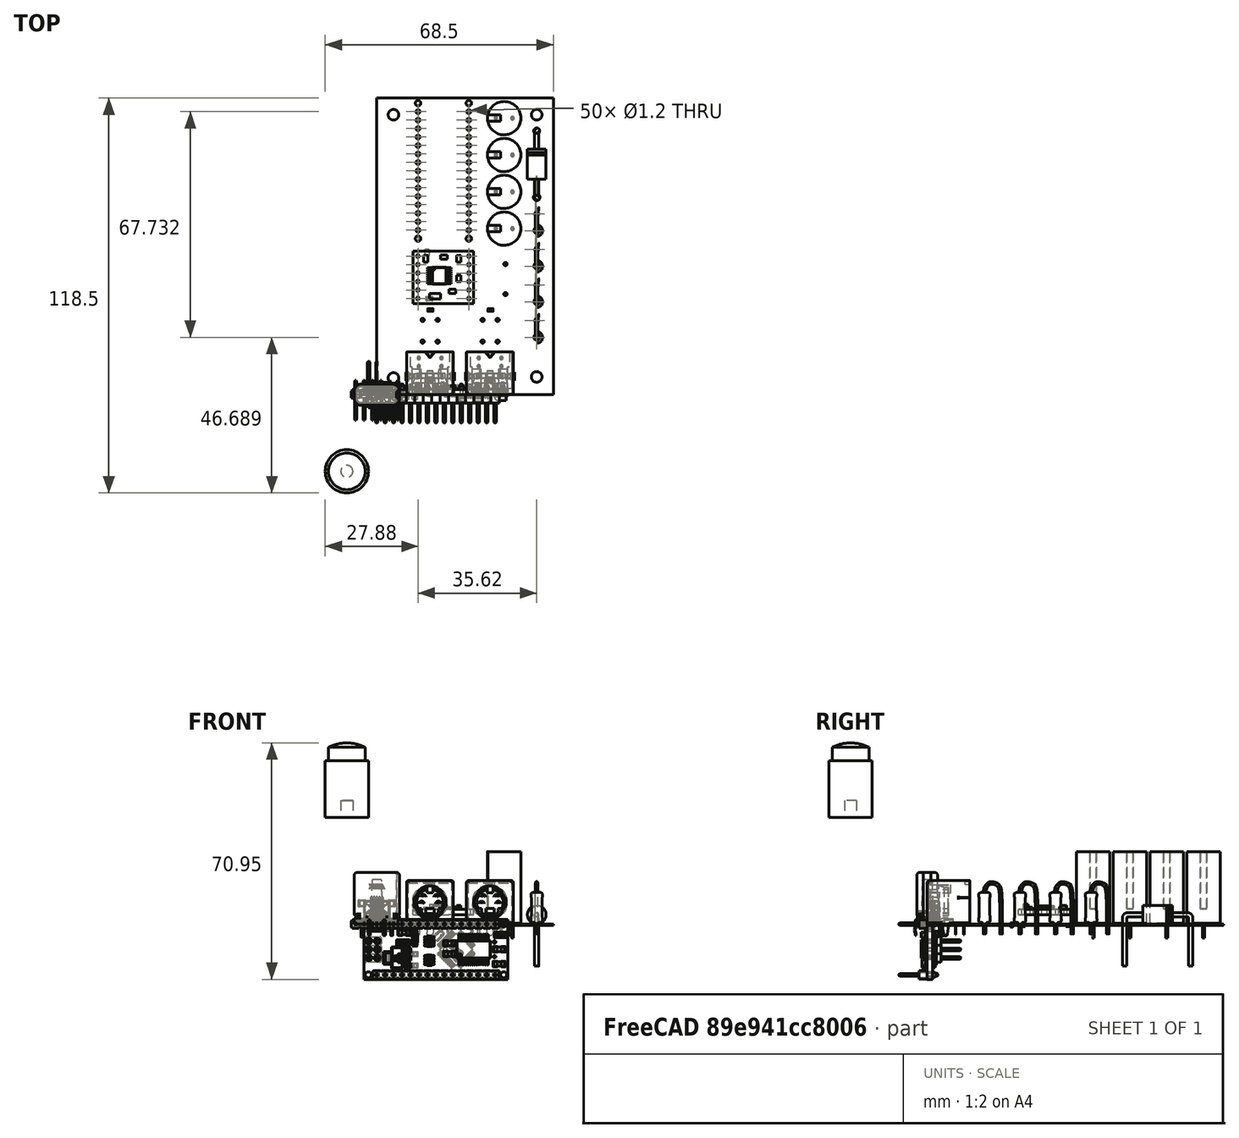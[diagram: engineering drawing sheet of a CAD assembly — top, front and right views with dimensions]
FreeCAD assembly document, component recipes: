
FREECAD ASSEMBLY — COMPONENT RECIPES ("box")

This assembly document has 7 components, labeled P0..P6 below (a component is one placed body or linked part). 6 of them carry a construction recipe — the FreeCAD feature program that regenerates the part from scratch, quoted from this document or its linked companion documents; the rest are supplied as boundary geometry only. No exploded tour is included for this assembly.
COMPONENT P0 — recipe-attached ("Back001", modeled in this document).
Construction recipe (the document's own serialized feature program — sketch geometry with constraints, then the solid features built on it; lengths are millimeters unless a unit is written):

FEATURE [PartDesign::Plane] DatumPlane001
  AttachmentSupport = -> [Mirrored002]
  Length = 77.6965
  MapMode = 5
  Placement = pos=(0,-47,-3.95e-14) rot=(1,0,0;1.5708rad)
  ResizeMode = 0
  Width = 74.6965
FEATURE [Sketcher::SketchObject] Sketch010
  ArcFitTolerance = 0
  AttachmentSupport = -> [DatumPlane001]
  FullyConstrained = true
  MakeInternals = false
  MapMode = 5
  Placement = pos=(0,-47,-3.95e-14) rot=(1,0,0;1.5708rad)
  sketch-geometry (8):
    g0: LineSegment StartX=-32.5 StartY=37 StartZ=0 EndX=-32.5 EndY=2 EndZ=0
    g1: LineSegment StartX=-32.5 StartY=2 StartZ=0 EndX=32.5 EndY=2 EndZ=0
    g2: LineSegment StartX=32.5 StartY=2 StartZ=0 EndX=32.5 EndY=37 EndZ=0
    g3: LineSegment StartX=32.5 StartY=37 StartZ=0 EndX=-32.5 EndY=37 EndZ=0
    g4: LineSegment StartX=0 StartY=29 StartZ=0 EndX=0 EndY=19 EndZ=0
    g5: LineSegment StartX=0 StartY=19 StartZ=0 EndX=13 EndY=19 EndZ=0
    g6: LineSegment StartX=13 StartY=19 StartZ=0 EndX=13 EndY=29 EndZ=0
    g7: LineSegment StartX=13 StartY=29 StartZ=0 EndX=0 EndY=29 EndZ=0
  constraints (23):
    c: Coincident(g0,g1)
    c: Coincident(g1,g2)
    c: Coincident(g2,g3)
    c: Coincident(g3,g0)
    c: Vertical(g0)
    c: Vertical(g2)
    c: Horizontal(g1)
    c: Symmetric(g0,g2,g-2)
    c: DistanceY(g-1,g0) = 2
    c: DistanceX(g3,g3) = 65
    c: DistanceY(g0,g0) = 35
    c: Coincident(g4,g5)
    c: Coincident(g5,g6)
    c: Coincident(g6,g7)
    c: Coincident(g7,g4)
    c: Vertical(g4)
    c: Vertical(g6)
    c: Horizontal(g5)
    c: Horizontal(g7)
    c: DistanceX(g7,g7) = 13
    c: DistanceY(g6,g6) = 10
    c: DistanceY(g-1,g4) = 19
    c: PointOnObject(g4,g-2)
FEATURE [PartDesign::Pad] Pad003
  Direction = (0,-1,2e-16)
  Length = 1.5
  Length2 = 10
  Placement = pos=(0,-47,-3.94e-14) rot=(1,0,0;1.5708rad)
  Profile = -> Sketch010
  ReferenceAxis = -> Sketch010 [N_Axis]
  Refine = true
  Suppressed = false
  Type = 0
FEATURE [PartDesign::Fillet] Fillet003
  Base = -> Pad003 [Edge1,Edge8,Edge5,Edge2,Edge13,Edge20,Edge14,Edge17]
  BaseFeature = -> Pad003
  Placement = pos=(0,-47,-3.94e-14) rot=(1,0,0;1.5708rad)
  Radius = 2
  Refine = true
  SupportTransform = false
  Suppressed = false
  UseAllEdges = false
FEATURE [Sketcher::SketchObject] Sketch019
  ArcFitTolerance = 1e-06
  AttachmentSupport = -> [Fillet003]
  FullyConstrained = true
  MakeInternals = false
  MapMode = 5
  Placement = pos=(0,-48.5,-3.94e-14) rot=(1,0,0;1.5708rad)
  sketch-geometry (6):
    g0: ArcOfCircle CenterX=23 CenterY=24 CenterZ=0 NormalX=0 NormalY=0 NormalZ=1 AngleXU=0 Radius=4.8 StartAngle=5.29807 EndAngle=10.4099
    g1: Circle [constr] CenterX=23 CenterY=24 CenterZ=0 NormalX=0 NormalY=0 NormalZ=1 AngleXU=0 Radius=6.325
    g2: LineSegment StartX=20.3467 StartY=20 StartZ=0 EndX=25.6533 EndY=20 EndZ=0
    g3: Circle [constr] CenterX=-23 CenterY=24 CenterZ=0 NormalX=0 NormalY=0 NormalZ=1 AngleXU=0 Radius=6.325
    g4: ArcOfCircle CenterX=-23 CenterY=24 CenterZ=0 NormalX=0 NormalY=0 NormalZ=1 AngleXU=0 Radius=4.8 StartAngle=5.29807 EndAngle=10.4099
    g5: LineSegment StartX=-25.6533 StartY=20 StartZ=0 EndX=-20.3467 EndY=20 EndZ=0
  constraints (18):
    c: Diameter(g0) = 9.6
    c: Diameter(g1) = 12.65
    c: Coincident(g1,g0)
    c: Distance(g0,g2) = 4
    c: DistanceY(g-1,g0) = 24
    c: DistanceX(g-1,g0) = 23
    c: Coincident(g0,g2)
    c: Coincident(g0,g2)
    c: Coincident(g4,g3)
    c: Equal(g4,g0)
    c: Equal(g3,g1)
    c: Horizontal(g3,g0)
    c: Horizontal(g5)
    c: Horizontal(g5,g0)
    c: Coincident(g4,g5)
    c: Coincident(g4,g5)
    c: DistanceX(g3,g-1) = 23
    c: Horizontal(g2)
FEATURE [PartDesign::Pocket] Pocket010
  BaseFeature = -> Fillet003
  Direction = (0,1,-2e-16)
  Length = 5
  Length2 = 5
  Placement = pos=(0,-47,-3.94e-14) rot=(1,0,0;1.5708rad)
  Profile = -> Sketch019
  ReferenceAxis = -> Sketch019 [N_Axis]
  Refine = true
  Suppressed = false
  Type = 1
FEATURE [PartDesign::Body] Body002  label="Back"
  AllowCompound = false
  Group = -> [DatumPlane001,Sketch010,Pad003,Fillet003,Sketch019,Pocket010]
  Origin = -> Origin052
  Tip = -> Pocket010
COMPONENT P1 — recipe-attached ("Bottom001", modeled in this document).
Construction recipe (the document's own serialized feature program — sketch geometry with constraints, then the solid features built on it; lengths are millimeters unless a unit is written):

FEATURE [Sketcher::SketchObject] Sketch
  ArcFitTolerance = 0
  AttachmentSupport = -> [XY_Plane050]
  FullyConstrained = true
  MakeInternals = false
  MapMode = 5
  sketch-geometry (4):
    g0: LineSegment StartX=-35 StartY=51 StartZ=0 EndX=-35 EndY=-51 EndZ=0
    g1: LineSegment StartX=-35 StartY=-51 StartZ=0 EndX=35 EndY=-51 EndZ=0
    g2: LineSegment StartX=35 StartY=-51 StartZ=0 EndX=35 EndY=51 EndZ=0
    g3: LineSegment StartX=35 StartY=51 StartZ=0 EndX=-35 EndY=51 EndZ=0
  constraints (10):
    c: Coincident(g0,g1)
    c: Coincident(g1,g2)
    c: Coincident(g2,g3)
    c: Coincident(g3,g0)
    c: Vertical(g2)
    c: Horizontal(g3)
    c: Distance(g0,g2) = 70
    c: Distance(g1,g3) = 102
    c: Symmetric(g1,g0,g-2)
    c: Symmetric(g0,g0,g-1)
FEATURE [PartDesign::Pad] Pad
  Direction = (0,0,1)
  Length = 20
  Length2 = 10
  Profile = -> Sketch
  ReferenceAxis = -> Sketch [N_Axis]
  Refine = true
  Suppressed = false
  Type = 0
FEATURE [Sketcher::SketchObject] Sketch001
  ArcFitTolerance = 0
  AttachmentSupport = -> [Pad]
  FullyConstrained = true
  MakeInternals = false
  MapMode = 5
  Placement = pos=(0,0,20) rot=(0,0,1;0rad)
  sketch-geometry (4):
    g0: LineSegment StartX=-32.5 StartY=45 StartZ=0 EndX=-32.5 EndY=-45 EndZ=0
    g1: LineSegment StartX=-32.5 StartY=-45 StartZ=0 EndX=32.5 EndY=-45 EndZ=0
    g2: LineSegment StartX=32.5 StartY=-45 StartZ=0 EndX=32.5 EndY=45 EndZ=0
    g3: LineSegment StartX=32.5 StartY=45 StartZ=0 EndX=-32.5 EndY=45 EndZ=0
  constraints (10):
    c: Coincident(g0,g1)
    c: Coincident(g1,g2)
    c: Coincident(g2,g3)
    c: Coincident(g3,g0)
    c: Vertical(g2)
    c: Horizontal(g1)
    c: Symmetric(g0,g2,g-2)
    c: Symmetric(g0,g0,g-1)
    c: DistanceX(g3,g3) = 65
    c: DistanceY(g2,g2) = 90
FEATURE [PartDesign::Pocket] Pocket
  BaseFeature = -> Pad
  Direction = (0,0,-1)
  Length = 18
  Length2 = 5
  Profile = -> Sketch001
  ReferenceAxis = -> Sketch001 [N_Axis]
  Refine = true
  Suppressed = false
  Type = 0
FEATURE [Sketcher::SketchObject] Sketch002
  ArcFitTolerance = 0
  AttachmentSupport = -> [Pocket]
  ExternalGeometry = -> [Pocket]
  FullyConstrained = true
  MakeInternals = false
  MapMode = 5
  Placement = pos=(0,51,0) rot=(0,0.707107,0.707107;3.14159rad)
  sketch-geometry (4):
    g0: LineSegment StartX=-31 StartY=20 StartZ=0 EndX=-31 EndY=4 EndZ=0
    g1: LineSegment StartX=-31 StartY=4 StartZ=0 EndX=31 EndY=4 EndZ=0
    g2: LineSegment StartX=31 StartY=4 StartZ=0 EndX=31 EndY=20 EndZ=0
    g3: LineSegment StartX=31 StartY=20 StartZ=0 EndX=-31 EndY=20 EndZ=0
  constraints (11):
    c: Coincident(g0,g1)
    c: Coincident(g1,g2)
    c: Coincident(g2,g3)
    c: Coincident(g3,g0)
    c: Vertical(g0)
    c: Vertical(g2)
    c: Horizontal(g1)
    c: PointOnObject(g0,g-3)
    c: Symmetric(g2,g0,g-2)
    c: DistanceY(g-1,g0) = 4
    c: Distance(g-3,g0) = 4
FEATURE [PartDesign::Pocket] Pocket001
  BaseFeature = -> Pocket
  Direction = (0,-1,2e-16)
  Length = 5
  Length2 = 5
  Profile = -> Sketch002
  ReferenceAxis = -> Sketch002 [N_Axis]
  Refine = true
  Suppressed = false
  Type = 1
FEATURE [Sketcher::SketchObject] Sketch003
  ArcFitTolerance = 0
  AttachmentSupport = -> [Pocket001]
  ExternalGeometry = -> [Pocket001]
  FullyConstrained = true
  MakeInternals = false
  MapMode = 5
  Placement = pos=(0,51,0) rot=(0,0.707107,0.707107;3.14159rad)
  sketch-geometry (4):
    g0: LineSegment StartX=-33 StartY=20 StartZ=0 EndX=-33 EndY=2 EndZ=0
    g1: LineSegment StartX=-33 StartY=2 StartZ=0 EndX=33 EndY=2 EndZ=0
    g2: LineSegment StartX=33 StartY=2 StartZ=0 EndX=33 EndY=20 EndZ=0
    g3: LineSegment StartX=33 StartY=20 StartZ=0 EndX=-33 EndY=20 EndZ=0
  constraints (11):
    c: Coincident(g0,g1)
    c: Coincident(g1,g2)
    c: Coincident(g2,g3)
    c: Coincident(g3,g0)
    c: Vertical(g0)
    c: Vertical(g2)
    c: Horizontal(g1)
    c: Symmetric(g0,g2,g-2)
    c: DistanceX(g-3,g0) = 2
    c: PointOnObject(g0,g-3)
    c: Distance(g0,g-1) = 2
FEATURE [PartDesign::Pocket] Pocket002
  BaseFeature = -> Pocket001
  Direction = (0,-1,2e-16)
  Length = 4
  Length2 = -2
  Profile = -> Sketch003
  ReferenceAxis = -> Sketch003 [N_Axis]
  Refine = true
  Suppressed = false
  Type = 4
FEATURE [PartDesign::Mirrored] Mirrored
  BaseFeature = -> Pocket002
  MirrorPlane = -> XZ_Plane050
  Originals = -> [Pocket002]
  Refine = true
  Suppressed = false
  TransformMode = 0
FEATURE [Sketcher::SketchObject] Sketch004
  ArcFitTolerance = 0
  AttachmentSupport = -> [Mirrored]
  FullyConstrained = true
  MakeInternals = false
  MapMode = 5
  Placement = pos=(0,0,2) rot=(0,0,1;0rad)
  sketch-geometry (8):
    g0: Circle CenterX=-21.5 CenterY=39.5 CenterZ=0 NormalX=0 NormalY=0 NormalZ=1 AngleXU=0 Radius=3
    g1: Circle CenterX=21.5 CenterY=39.5 CenterZ=0 NormalX=0 NormalY=0 NormalZ=1 AngleXU=0 Radius=3
    g2: Circle CenterX=-21.5 CenterY=-39.5 CenterZ=0 NormalX=0 NormalY=0 NormalZ=1 AngleXU=0 Radius=3
    g3: Circle CenterX=21.5 CenterY=-39.5 CenterZ=0 NormalX=0 NormalY=0 NormalZ=1 AngleXU=0 Radius=3
    g4: Circle CenterX=-21.5 CenterY=39.5 CenterZ=0 NormalX=0 NormalY=0 NormalZ=1 AngleXU=0 Radius=1.25
    g5: Circle CenterX=21.5 CenterY=39.5 CenterZ=0 NormalX=0 NormalY=0 NormalZ=1 AngleXU=0 Radius=1.25
    g6: Circle CenterX=-21.5 CenterY=-39.5 CenterZ=0 NormalX=0 NormalY=0 NormalZ=1 AngleXU=0 Radius=1.25
    g7: Circle CenterX=21.5 CenterY=-39.5 CenterZ=0 NormalX=0 NormalY=0 NormalZ=1 AngleXU=0 Radius=1.25
  constraints (17):
    c: Equal(g0,g1)
    c: Equal(g1,g2)
    c: Equal(g2,g3)
    c: Symmetric(g2,g3,g-2)
    c: Symmetric(g0,g1,g-2)
    c: Symmetric(g0,g2,g-1)
    c: DistanceY(g2,g0) = 79
    c: DistanceX(g0,g1) = 43
    c: Diameter(g0) = 6
    c: Coincident(g4,g0)
    c: Coincident(g5,g1)
    c: Coincident(g6,g2)
    c: Coincident(g7,g3)
    c: Equal(g5,g4)
    c: Equal(g4,g6)
    c: Equal(g6,g7)
    c: Diameter(g4) = 2.5
FEATURE [PartDesign::Pad] Pad001
  BaseFeature = -> Mirrored
  Direction = (0,0,1)
  Length = 8
  Length2 = 10
  Profile = -> Sketch004
  ReferenceAxis = -> Sketch004 [N_Axis]
  Refine = true
  Suppressed = false
  Type = 0
FEATURE [PartDesign::Chamfer] Chamfer
  Angle = 45
  Base = -> Pad001 [Edge98,Edge97,Edge99,Edge100]
  BaseFeature = -> Pad001
  ChamferType = 0
  FlipDirection = false
  Refine = true
  Size = 2
  Size2 = 1
  SupportTransform = false
  Suppressed = false
  UseAllEdges = false
FEATURE [PartDesign::Fillet] Fillet
  Base = -> Chamfer [Edge106,Edge103,Edge112,Edge107,Edge19,Edge11,Edge25,Edge12]
  BaseFeature = -> Chamfer
  Radius = 1
  Refine = true
  SupportTransform = false
  Suppressed = false
  UseAllEdges = false
FEATURE [PartDesign::Chamfer] Chamfer001
  Angle = 45
  Base = -> Fillet [Face53]
  BaseFeature = -> Fillet
  ChamferType = 0
  FlipDirection = false
  Refine = true
  Size = 2
  Size2 = 1
  SupportTransform = false
  Suppressed = false
  UseAllEdges = false
FEATURE [PartDesign::Fillet] Fillet001
  Base = -> Chamfer001 [Edge112]
  BaseFeature = -> Chamfer001
  Radius = 1
  Refine = true
  SupportTransform = false
  Suppressed = false
  UseAllEdges = false
FEATURE [Sketcher::SketchObject] Sketch005
  ArcFitTolerance = 0
  AttachmentSupport = -> [Fillet001]
  ExternalGeometry = -> [Fillet001]
  FullyConstrained = true
  MakeInternals = false
  MapMode = 5
  Placement = pos=(0,0,20) rot=(0,0,1;0rad)
  sketch-geometry (4):
    g0: LineSegment StartX=31.75 StartY=40 StartZ=0 EndX=31.75 EndY=-40 EndZ=0
    g1: LineSegment StartX=31.75 StartY=-40 StartZ=0 EndX=30.75 EndY=-40 EndZ=0
    g2: LineSegment StartX=30.75 StartY=-40 StartZ=0 EndX=30.75 EndY=40 EndZ=0
    g3: LineSegment StartX=30.75 StartY=40 StartZ=0 EndX=31.75 EndY=40 EndZ=0
  constraints (11):
    c: Coincident(g0,g1)
    c: Coincident(g1,g2)
    c: Coincident(g2,g3)
    c: Coincident(g3,g0)
    c: Vertical(g2)
    c: Horizontal(g1)
    c: Horizontal(g3)
    c: Distance(g0,g2) = 1
    c: Distance(g1,g3) = 80
    c: Symmetric(g0,g0,g-1)
    c: DistanceX(g-3,g0) = 0.75
FEATURE [PartDesign::Pocket] Pocket003
  BaseFeature = -> Fillet001
  Direction = (0,0,-1)
  Length = 1
  Length2 = 5
  Profile = -> Sketch005
  ReferenceAxis = -> Sketch005 [N_Axis]
  Refine = true
  Suppressed = false
  Type = 0
FEATURE [PartDesign::Mirrored] Mirrored001
  BaseFeature = -> Pocket003
  MirrorPlane = -> Sketch005 [V_Axis]
  Originals = -> [Pocket003]
  Refine = true
  Suppressed = false
  TransformMode = 0
FEATURE [Sketcher::SketchObject] Sketch006
  ArcFitTolerance = 0
  AttachmentSupport = -> [Mirrored001]
  ExternalGeometry = -> [Mirrored001]
  FullyConstrained = true
  MakeInternals = false
  MapMode = 5
  Placement = pos=(35,0,0) rot=(0.57735,0.57735,0.57735;2.0944rad)
  sketch-geometry (2):
    g0: Circle CenterX=-30 CenterY=16 CenterZ=0 NormalX=0 NormalY=0 NormalZ=1 AngleXU=0 Radius=1.25
    g1: Circle CenterX=30 CenterY=16 CenterZ=0 NormalX=0 NormalY=0 NormalZ=1 AngleXU=0 Radius=1.25
  constraints (5):
    c: Equal(g1,g0)
    c: Symmetric(g0,g1,g-2)
    c: DistanceX(g0,g1) = 60
    c: Diameter(g0) = 2.5
    c: DistanceY(g-1,g1) = 16
FEATURE [PartDesign::Pocket] Pocket004
  BaseFeature = -> Mirrored001
  Direction = (-1,0,0)
  Length = 5
  Length2 = 5
  Profile = -> Sketch006
  ReferenceAxis = -> Sketch006 [N_Axis]
  Refine = true
  Suppressed = false
  Type = 1
FEATURE [PartDesign::Mirrored] Mirrored002
  BaseFeature = -> Pocket004
  MirrorPlane = -> YZ_Plane050
  Originals = -> [Pocket004]
  Refine = true
  Suppressed = false
  TransformMode = 0
FEATURE [PartDesign::Body] Body  label="Bottom"
  AllowCompound = false
  Group = -> [Sketch,Pad,Sketch001,Pocket,Sketch002,Pocket001,Sketch003,Pocket002,Mirrored,Sketch004,Pad001,Chamfer,Fillet,Chamfer001,Fillet001,Sketch005,Pocket003,Mirrored001,Sketch006,Pocket004,Mirrored002]
  Origin = -> Origin050
  Tip = -> Mirrored002
COMPONENT P2 — recipe-attached ("Front001", modeled in this document).
Construction recipe (the document's own serialized feature program — sketch geometry with constraints, then the solid features built on it; lengths are millimeters unless a unit is written):

FEATURE [PartDesign::Plane] DatumPlane
  AttachmentSupport = -> [Mirrored002]
  Length = 77.6965
  MapMode = 5
  Placement = pos=(0,-45,0) rot=(0,0.707107,0.707107;3.14159rad)
  ResizeMode = 0
  Width = 74.6965
FEATURE [Sketcher::SketchObject] Sketch007
  ArcFitTolerance = 0
  AttachmentSupport = -> [DatumPlane]
  FullyConstrained = true
  MakeInternals = false
  MapMode = 5
  Placement = pos=(0,-45,0) rot=(0,0.707107,0.707107;3.14159rad)
  sketch-geometry (4):
    g0: LineSegment StartX=-32.5 StartY=37 StartZ=0 EndX=-32.5 EndY=2 EndZ=0
    g1: LineSegment StartX=-32.5 StartY=2 StartZ=0 EndX=32.5 EndY=2 EndZ=0
    g2: LineSegment StartX=32.5 StartY=2 StartZ=0 EndX=32.5 EndY=37 EndZ=0
    g3: LineSegment StartX=32.5 StartY=37 StartZ=0 EndX=-32.5 EndY=37 EndZ=0
  constraints (11):
    c: Coincident(g0,g1)
    c: Coincident(g1,g2)
    c: Coincident(g2,g3)
    c: Coincident(g3,g0)
    c: Vertical(g0)
    c: Vertical(g2)
    c: Horizontal(g1)
    c: Symmetric(g0,g2,g-2)
    c: DistanceY(g0,g0) = 35
    c: DistanceX(g1,g1) = 65
    c: Distance(g0,g-1) = 2
FEATURE [PartDesign::Pad] Pad002
  Direction = (0,1,-2e-16)
  Length = 1.5
  Length2 = 10
  Placement = pos=(0,-45,0) rot=(0,0.707107,0.707107;3.14159rad)
  Profile = -> Sketch007
  ReferenceAxis = -> Sketch007 [N_Axis]
  Refine = true
  Suppressed = false
  Type = 0
FEATURE [Sketcher::SketchObject] Sketch008
  ArcFitTolerance = 0
  AttachmentSupport = -> [Pad002]
  FullyConstrained = true
  MakeInternals = false
  MapMode = 5
  Placement = pos=(0,-43.5,0) rot=(0,0.707107,0.707107;3.14159rad)
  sketch-geometry (8):
    g0: LineSegment StartX=-18 StartY=24 StartZ=0 EndX=-18 EndY=10 EndZ=0
    g1: LineSegment StartX=-18 StartY=10 StartZ=0 EndX=-3 EndY=10 EndZ=0
    g2: LineSegment StartX=-3 StartY=10 StartZ=0 EndX=-3 EndY=24 EndZ=0
    g3: LineSegment StartX=-3 StartY=24 StartZ=0 EndX=-18 EndY=24 EndZ=0
    g4: LineSegment StartX=0 StartY=10 StartZ=0 EndX=15 EndY=10 EndZ=0
    g5: LineSegment StartX=15 StartY=10 StartZ=0 EndX=15 EndY=24 EndZ=0
    g6: LineSegment StartX=15 StartY=24 StartZ=0 EndX=0 EndY=24 EndZ=0
    g7: LineSegment StartX=0 StartY=24 StartZ=0 EndX=0 EndY=10 EndZ=0
  constraints (24):
    c: Coincident(g0,g1)
    c: Coincident(g1,g2)
    c: Coincident(g2,g3)
    c: Coincident(g3,g0)
    c: Vertical(g0)
    c: Vertical(g2)
    c: Horizontal(g1)
    c: Horizontal(g3)
    c: Coincident(g4,g5)
    c: Coincident(g5,g6)
    c: Coincident(g6,g7)
    c: Coincident(g7,g4)
    c: Horizontal(g4)
    c: Horizontal(g6)
    c: Vertical(g5)
    c: Vertical(g7)
    c: Equal(g3,g6)
    c: Equal(g0,g7)
    c: Horizontal(g0,g4)
    c: DistanceY(g0,g0) = 14
    c: DistanceX(g3,g3) = 15
    c: DistanceY(g-1,g0) = 10
    c: DistanceX(g0,g-1) = 18
    c: DistanceX(g2,g6) = 3
FEATURE [PartDesign::Pocket] Pocket005
  BaseFeature = -> Pad002
  Direction = (0,-1,2e-16)
  Length = 5
  Length2 = 5
  Placement = pos=(0,-45,0) rot=(0,0.707107,0.707107;3.14159rad)
  Profile = -> Sketch008
  ReferenceAxis = -> Sketch008 [N_Axis]
  Refine = true
  Suppressed = false
  Type = 1
FEATURE [PartDesign::Fillet] Fillet002
  Base = -> Pocket005 [Edge1,Edge2,Edge8,Edge5,Edge36,Edge33,Edge35,Edge34,Edge31,Edge30,Edge32,Edge29]
  BaseFeature = -> Pocket005
  Placement = pos=(0,-45,0) rot=(0,0.707107,0.707107;3.14159rad)
  Radius = 2
  Refine = true
  SupportTransform = false
  Suppressed = false
  UseAllEdges = false
FEATURE [Sketcher::SketchObject] Sketch009
  ArcFitTolerance = 0
  AttachmentSupport = -> [Fillet002]
  FullyConstrained = true
  MakeInternals = false
  MapMode = 5
  Placement = pos=(0,-43.5,0) rot=(0,0.707107,0.707107;3.14159rad)
FEATURE [PartDesign::Body] Body001  label="Front"
  AllowCompound = false
  Group = -> [DatumPlane,Sketch007,Pad002,Sketch008,Pocket005,Fillet002,Sketch009]
  Origin = -> Origin051
  Tip = -> Fillet002
COMPONENT P3 — geometry summary ("PCB001"; no construction recipe available for this part):
  bounding box: 90.5 x 53.0 x 34.4 mm
  tessellated surface: 704,668 triangles
  volume: 18010 mm^3 (11% of its bounding box)
COMPONENT P4 — recipe-attached ("Top001", modeled in this document).
Construction recipe (the document's own serialized feature program — sketch geometry with constraints, then the solid features built on it; lengths are millimeters unless a unit is written):

FEATURE [Sketcher::SketchObject] Sketch011
  ArcFitTolerance = 0
  AttachmentSupport = -> [XY_Plane053]
  FullyConstrained = true
  MakeInternals = false
  MapMode = 5
  sketch-geometry (4):
    g0: LineSegment StartX=-35 StartY=51 StartZ=0 EndX=-35 EndY=-51 EndZ=0
    g1: LineSegment StartX=-35 StartY=-51 StartZ=0 EndX=35 EndY=-51 EndZ=0
    g2: LineSegment StartX=35 StartY=-51 StartZ=0 EndX=35 EndY=51 EndZ=0
    g3: LineSegment StartX=35 StartY=51 StartZ=0 EndX=-35 EndY=51 EndZ=0
  constraints (10):
    c: Coincident(g0,g1)
    c: Coincident(g1,g2)
    c: Coincident(g2,g3)
    c: Coincident(g3,g0)
    c: Vertical(g2)
    c: Horizontal(g3)
    c: Distance(g0,g2) = 70
    c: Distance(g1,g3) = 102
    c: Symmetric(g1,g0,g-2)
    c: Symmetric(g0,g0,g-1)
FEATURE [PartDesign::Pad] Pad004
  Direction = (0,0,1)
  Length = 20
  Length2 = 10
  Profile = -> Sketch011
  ReferenceAxis = -> Sketch011 [N_Axis]
  Refine = true
  Suppressed = false
  Type = 0
FEATURE [Sketcher::SketchObject] Sketch012
  ArcFitTolerance = 0
  AttachmentSupport = -> [Pad004]
  FullyConstrained = true
  MakeInternals = false
  MapMode = 5
  Placement = pos=(0,0,20) rot=(0,0,1;0rad)
  sketch-geometry (4):
    g0: LineSegment StartX=-32.5 StartY=45 StartZ=0 EndX=-32.5 EndY=-45 EndZ=0
    g1: LineSegment StartX=-32.5 StartY=-45 StartZ=0 EndX=32.5 EndY=-45 EndZ=0
    g2: LineSegment StartX=32.5 StartY=-45 StartZ=0 EndX=32.5 EndY=45 EndZ=0
    g3: LineSegment StartX=32.5 StartY=45 StartZ=0 EndX=-32.5 EndY=45 EndZ=0
  constraints (10):
    c: Coincident(g0,g1)
    c: Coincident(g1,g2)
    c: Coincident(g2,g3)
    c: Coincident(g3,g0)
    c: Vertical(g2)
    c: Horizontal(g1)
    c: Symmetric(g0,g2,g-2)
    c: Symmetric(g0,g0,g-1)
    c: DistanceX(g3,g3) = 65
    c: DistanceY(g2,g2) = 90
FEATURE [PartDesign::Pocket] Pocket006
  BaseFeature = -> Pad004
  Direction = (0,0,-1)
  Length = 18
  Length2 = 5
  Profile = -> Sketch012
  ReferenceAxis = -> Sketch012 [N_Axis]
  Refine = true
  Suppressed = false
  Type = 0
FEATURE [Sketcher::SketchObject] Sketch013
  ArcFitTolerance = 0
  AttachmentSupport = -> [Pocket006]
  ExternalGeometry = -> [Pocket006]
  FullyConstrained = true
  MakeInternals = false
  MapMode = 5
  Placement = pos=(0,51,0) rot=(0,0.707107,0.707107;3.14159rad)
  sketch-geometry (4):
    g0: LineSegment StartX=-31 StartY=20 StartZ=0 EndX=-31 EndY=4 EndZ=0
    g1: LineSegment StartX=-31 StartY=4 StartZ=0 EndX=31 EndY=4 EndZ=0
    g2: LineSegment StartX=31 StartY=4 StartZ=0 EndX=31 EndY=20 EndZ=0
    g3: LineSegment StartX=31 StartY=20 StartZ=0 EndX=-31 EndY=20 EndZ=0
  constraints (11):
    c: Coincident(g0,g1)
    c: Coincident(g1,g2)
    c: Coincident(g2,g3)
    c: Coincident(g3,g0)
    c: Vertical(g0)
    c: Vertical(g2)
    c: Horizontal(g1)
    c: PointOnObject(g0,g-3)
    c: Symmetric(g2,g0,g-2)
    c: DistanceY(g-1,g0) = 4
    c: Distance(g-3,g0) = 4
FEATURE [PartDesign::Pocket] Pocket007
  BaseFeature = -> Pocket006
  Direction = (0,-1,2e-16)
  Length = 5
  Length2 = 5
  Profile = -> Sketch013
  ReferenceAxis = -> Sketch013 [N_Axis]
  Refine = true
  Suppressed = false
  Type = 1
FEATURE [Sketcher::SketchObject] Sketch014
  ArcFitTolerance = 0
  AttachmentSupport = -> [Pocket007]
  ExternalGeometry = -> [Pocket007]
  FullyConstrained = true
  MakeInternals = false
  MapMode = 5
  Placement = pos=(0,51,0) rot=(0,0.707107,0.707107;3.14159rad)
  sketch-geometry (4):
    g0: LineSegment StartX=-33 StartY=20 StartZ=0 EndX=-33 EndY=2 EndZ=0
    g1: LineSegment StartX=-33 StartY=2 StartZ=0 EndX=33 EndY=2 EndZ=0
    g2: LineSegment StartX=33 StartY=2 StartZ=0 EndX=33 EndY=20 EndZ=0
    g3: LineSegment StartX=33 StartY=20 StartZ=0 EndX=-33 EndY=20 EndZ=0
  constraints (11):
    c: Coincident(g0,g1)
    c: Coincident(g1,g2)
    c: Coincident(g2,g3)
    c: Coincident(g3,g0)
    c: Vertical(g0)
    c: Vertical(g2)
    c: Horizontal(g1)
    c: Symmetric(g0,g2,g-2)
    c: DistanceX(g-3,g0) = 2
    c: PointOnObject(g0,g-3)
    c: Distance(g0,g-1) = 2
FEATURE [PartDesign::Pocket] Pocket008
  BaseFeature = -> Pocket007
  Direction = (0,-1,2e-16)
  Length = 4
  Length2 = -2
  Profile = -> Sketch014
  ReferenceAxis = -> Sketch014 [N_Axis]
  Refine = true
  Suppressed = false
  Type = 4
FEATURE [PartDesign::Mirrored] Mirrored003
  BaseFeature = -> Pocket008
  MirrorPlane = -> XZ_Plane053
  Originals = -> [Pocket008]
  Refine = true
  Suppressed = false
  TransformMode = 0
FEATURE [Sketcher::SketchObject] Sketch015
  ArcFitTolerance = 0
  AttachmentSupport = -> [Mirrored003]
  ExternalGeometry = -> [Mirrored003]
  FullyConstrained = true
  MakeInternals = false
  MapMode = 5
  Placement = pos=(0,0,20) rot=(0,0,1;0rad)
  sketch-geometry (4):
    g0: LineSegment StartX=-33.25 StartY=39 StartZ=0 EndX=-34.25 EndY=39 EndZ=0
    g1: LineSegment StartX=-34.25 StartY=39 StartZ=0 EndX=-34.25 EndY=-39 EndZ=0
    g2: LineSegment StartX=-34.25 StartY=-39 StartZ=0 EndX=-33.25 EndY=-39 EndZ=0
    g3: LineSegment StartX=-33.25 StartY=-39 StartZ=0 EndX=-33.25 EndY=39 EndZ=0
  constraints (11):
    c: Coincident(g0,g1)
    c: Coincident(g1,g2)
    c: Coincident(g2,g3)
    c: Coincident(g3,g0)
    c: Horizontal(g0)
    c: Horizontal(g2)
    c: Vertical(g3)
    c: Distance(g0,g0) = 1
    c: DistanceY(g1,g1) = 78
    c: Symmetric(g0,g1,g-1)
    c: Distance(g0,g-3) = 0.75
FEATURE [PartDesign::Pad] Pad005
  BaseFeature = -> Mirrored003
  Direction = (0,0,1)
  Length = 1
  Length2 = 10
  Profile = -> Sketch015
  ReferenceAxis = -> Sketch015 [N_Axis]
  Refine = true
  Suppressed = false
  Type = 0
FEATURE [PartDesign::Mirrored] Mirrored004
  BaseFeature = -> Pad005
  MirrorPlane = -> Sketch015 [V_Axis]
  Originals = -> [Pad005]
  Refine = true
  Suppressed = false
  TransformMode = 0
FEATURE [Sketcher::SketchObject] Sketch016
  ArcFitTolerance = 0
  AttachmentSupport = -> [Mirrored004]
  ExternalGeometry = -> [Mirrored004]
  FullyConstrained = true
  MakeInternals = false
  MapMode = 5
  Placement = pos=(32.5,0,0) rot=(0.57735,-0.57735,-0.57735;2.0944rad)
  sketch-geometry (8):
    g0: LineSegment StartX=-40 StartY=15 StartZ=0 EndX=-20 EndY=15 EndZ=0
    g1: LineSegment StartX=-20 StartY=15 StartZ=0 EndX=-20 EndY=20 EndZ=0
    g2: LineSegment StartX=-20 StartY=20 StartZ=0 EndX=-25 EndY=27 EndZ=0
    g3: LineSegment StartX=-25 StartY=27 StartZ=0 EndX=-35 EndY=27 EndZ=0
    g4: LineSegment StartX=-35 StartY=27 StartZ=0 EndX=-40 EndY=20 EndZ=0
    g5: LineSegment StartX=-40 StartY=20 StartZ=0 EndX=-40 EndY=15 EndZ=0
    g6: Circle CenterX=-30 CenterY=24 CenterZ=0 NormalX=0 NormalY=0 NormalZ=1 AngleXU=0 Radius=1
    g7: GeomPoint X=-30 Y=15 Z=0
  constraints (22):
    c: Coincident(g0,g1)
    c: Vertical(g1)
    c: Coincident(g1,g2)
    c: Coincident(g2,g3)
    c: Coincident(g3,g4)
    c: Coincident(g4,g5)
    c: Coincident(g5,g0)
    c: Vertical(g5)
    c: DistanceX(g0,g0) = 20
    c: DistanceX(g3,g3) = 10
    c: DistanceY(g-1,g0) = 15
    c: DistanceY(g-1,g3) = 27
    c: DistanceY(g5,g5) = 5
    c: Equal(g1,g5)
    c: Diameter(g6) = 2
    c: Distance(g6,g-3) = 4
    c: Equal(g2,g4)
    c: Horizontal(g0)
    c: Horizontal(g3)
    c: Symmetric(g0,g0,g7)
    c: Vertical(g6,g7)
    c: Distance(g7,g-2) = 30
FEATURE [PartDesign::Pad] Pad006
  BaseFeature = -> Mirrored004
  Direction = (-1,0,0)
  Length = 3
  Length2 = 10
  Profile = -> Sketch016
  ReferenceAxis = -> Sketch016 [N_Axis]
  Refine = true
  Suppressed = false
  Type = 0
FEATURE [PartDesign::Mirrored] Mirrored005
  MirrorPlane = -> XZ_Plane053
  Refine = true
  Suppressed = false
  TransformMode = 0
FEATURE [PartDesign::Mirrored] Mirrored006
  MirrorPlane = -> YZ_Plane053
  Refine = true
  Suppressed = false
  TransformMode = 0
FEATURE [PartDesign::MultiTransform] MultiTransform
  BaseFeature = -> Pad006
  Originals = -> [Pad006]
  Refine = true
  Suppressed = false
  TransformMode = 0
  Transformations = -> [Mirrored005,Mirrored006]
FEATURE [Sketcher::SketchObject] Sketch017
  ArcFitTolerance = 0
  AttachmentSupport = -> [MultiTransform]
  FullyConstrained = true
  MakeInternals = false
  MapMode = 5
  Placement = pos=(0,0,0) rot=(1,0,0;3.14159rad)
  sketch-geometry (2):
    g0: Circle CenterX=-7.5 CenterY=25.4 CenterZ=0 NormalX=0 NormalY=0 NormalZ=1 AngleXU=0 Radius=6
    g1: Circle CenterX=10.5 CenterY=25.4 CenterZ=0 NormalX=0 NormalY=0 NormalZ=1 AngleXU=0 Radius=6
  constraints (6):
    c: Equal(g0,g1)
    c: Horizontal(g0,g1)
    c: DistanceX(g0,g1) = 18
    c: DistanceY(g-1,g0) = 25.4
    c: DistanceX(g0,g-1) = 7.5
    c: Diameter(g0) = 12
FEATURE [PartDesign::Pocket] Pocket009
  BaseFeature = -> MultiTransform
  Direction = (0,0,1)
  Length = 5
  Length2 = 5
  Profile = -> Sketch017
  ReferenceAxis = -> Sketch017 [N_Axis]
  Refine = true
  Suppressed = false
  Type = 1
FEATURE [PartDesign::Chamfer] Chamfer002
  Angle = 45
  Base = -> Pocket009 [Edge3,Edge12,Edge19,Edge5]
  BaseFeature = -> Pocket009
  ChamferType = 0
  FlipDirection = false
  Refine = true
  Size = 2
  Size2 = 1
  SupportTransform = false
  Suppressed = false
  UseAllEdges = false
FEATURE [PartDesign::Fillet] Fillet004
  Base = -> Chamfer002 [Edge111,Edge99,Edge110,Edge128,Edge101,Edge149,Edge129,Edge100]
  BaseFeature = -> Chamfer002
  Radius = 1
  Refine = true
  SupportTransform = false
  Suppressed = false
  UseAllEdges = false
FEATURE [PartDesign::Fillet] Fillet005
  Base = -> Fillet004 [Edge79,Edge70,Edge72,Edge86]
  BaseFeature = -> Fillet004
  Radius = 1
  Refine = true
  SupportTransform = false
  Suppressed = false
  UseAllEdges = false
FEATURE [PartDesign::Chamfer] Chamfer003
  Angle = 45
  Base = -> Fillet005 [Edge213,Edge217,Edge94,Edge99]
  BaseFeature = -> Fillet005
  ChamferType = 0
  FlipDirection = false
  Refine = true
  Size = 2.9
  Size2 = 1
  SupportTransform = false
  Suppressed = false
  UseAllEdges = false
FEATURE [PartDesign::Chamfer] Chamfer004
  Angle = 45
  Base = -> Chamfer003 [Face72,Face102]
  BaseFeature = -> Chamfer003
  ChamferType = 0
  FlipDirection = false
  Refine = true
  Size = 0.49
  Size2 = 1
  SupportTransform = false
  Suppressed = false
  UseAllEdges = false
FEATURE [PartDesign::Body] Body003  label="Top"
  AllowCompound = false
  Group = -> [Sketch011,Pad004,Sketch012,Pocket006,Sketch013,Pocket007,Sketch014,Pocket008,Mirrored003,Sketch015,Pad005,Mirrored004,Sketch016,Pad006,MultiTransform,Mirrored005,Mirrored006,Sketch017,Pocket009,Chamfer002,Fillet004,Fillet005,Chamfer003,Chamfer004]
  Origin = -> Origin053
  Placement = pos=(0,0,40) rot=(0,1,0;3.14159rad)
  Tip = -> Chamfer004
COMPONENT P5 — recipe-attached ("bouton001", modeled in this document).
Construction recipe (the document's own serialized feature program — sketch geometry with constraints, then the solid features built on it; lengths are millimeters unless a unit is written):

FEATURE [Sketcher::SketchObject] Sketch018
  ArcFitTolerance = 0
  AttachmentSupport = -> [YZ_Plane054]
  FullyConstrained = true
  MakeInternals = false
  MapMode = 5
  Placement = pos=(0,0,0) rot=(0.57735,0.57735,0.57735;2.0944rad)
  sketch-geometry (7):
    g0: LineSegment StartX=1.8 StartY=0 StartZ=0 EndX=5.3 EndY=0 EndZ=0
    g1: ArcOfCircle CenterX=0 CenterY=14.9268 CenterZ=0 NormalX=0 NormalY=0 NormalZ=1 AngleXU=0 Radius=5.52324 StartAngle=0.0917729 EndAngle=1.5708
    g2: LineSegment StartX=0 StartY=20.45 StartZ=0 EndX=0 EndY=5 EndZ=0
    g3: LineSegment StartX=1.8 StartY=5 StartZ=0 EndX=1.8 EndY=0 EndZ=0
    g4: LineSegment StartX=0 StartY=5 StartZ=0 EndX=1.8 EndY=5 EndZ=0
    g5: LineSegment StartX=5.5 StartY=15.4329 StartZ=0 EndX=6 EndY=10 EndZ=0
    g6: LineSegment StartX=6 StartY=10 StartZ=0 EndX=5.3 EndY=0 EndZ=0
  constraints (21):
    c: PointOnObject(g0,g-1)
    c: Horizontal(g0)
    c: PointOnObject(g1,g-2)
    c: Coincident(g1,g2)
    c: PointOnObject(g2,g-2)
    c: Coincident(g3,g0)
    c: Coincident(g2,g4)
    c: Horizontal(g4)
    c: Vertical(g3)
    c: Distance(g0,g-2) = 1.8
    c: DistanceX(g-1,g1) = 5.5
    c: DistanceY(g-1,g2) = 5
    c: Coincident(g3,g4)
    c: DistanceY(g2,g1) = 15.45
    c: Coincident(g5,g6)
    c: Coincident(g6,g0)
    c: Distance(g0,g0) = 3.5
    c: Distance(g5,g2) = 6
    c: DistanceY(g-1,g5) = 10
    c: Tangent(g1,g5) = 1.5708
    c: Perpendicular(g1,g2)
FEATURE [PartDesign::Revolution] Revolution
  Angle = 360
  Angle2 = 60
  Axis = (0,0,1)
  Base = (0,0,0)
  Placement = pos=(0,0,0) rot=(1,1,1;2.0944rad)
  Profile = -> Sketch018
  ReferenceAxis = -> Sketch018 [V_Axis]
  Refine = true
  Reversed = true
  Suppressed = false
  Type = 0
FEATURE [PartDesign::Body] Body004  label="bouton"
  AllowCompound = false
  Group = -> [Sketch018,Revolution]
  Origin = -> Origin054
  Placement = pos=(-9,-23,32) rot=(0,0,1;0rad)
  Tip = -> Revolution
COMPONENT P6 — same part as P5; its construction recipe is shown at P5.
PROVENANCE & LICENSES
A FreeCAD (.FCStd) document from a public repository crawl; recipes are the document's own serialized feature recipes (and, for linked parts, companion documents' recipes).
License: lgpl-3.0.
